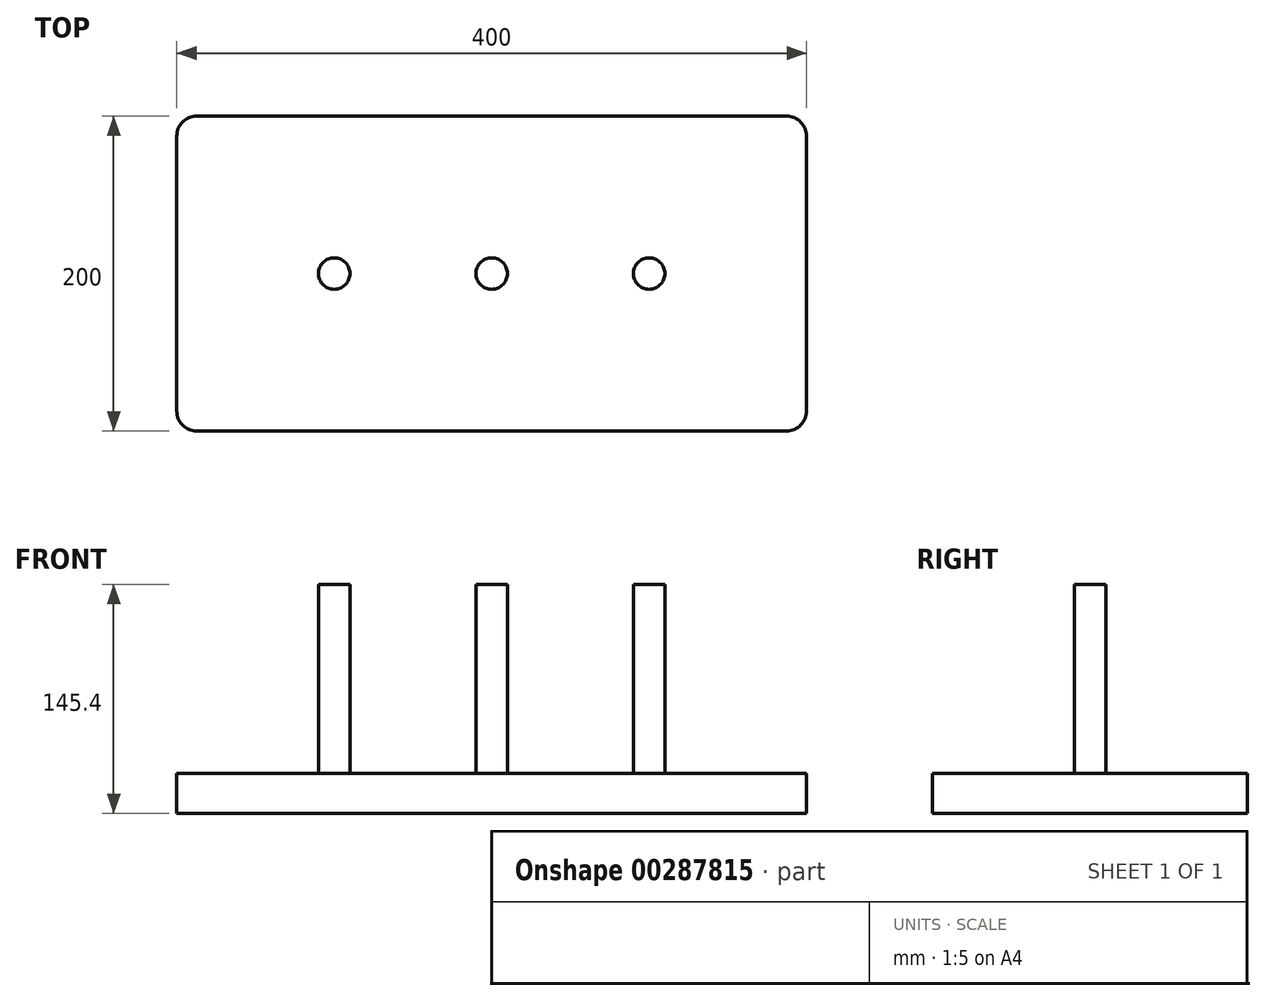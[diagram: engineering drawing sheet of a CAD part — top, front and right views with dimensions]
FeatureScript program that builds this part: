
annotation { "Feature Type Name" : "Feature", "Feature Type Description" : "" }
export const myFeature = defineFeature(function(context is Context, id is Id, definition is map)
    precondition{}
    {
        {
            var Q0;
            Q0=qCreatedBy(makeId("Top.planeOp"),FACE);
            var sketch = newSketch(context, id + "F0", { "sketchPlane" : qUnion([Q0])});
            skLineSegment(sketch, "E0.bottom", {"start": v(200, -100) * mm, "end": v(-200, -100) * mm});
            skLineSegment(sketch, "E0.top", {"start": v(200, 100) * mm, "end": v(-200, 100) * mm});
            skLineSegment(sketch, "E0.left", {"start": v(200, -100) * mm, "end": v(200, 100) * mm});
            skLineSegment(sketch, "E0.right", {"start": v(-200, -100) * mm, "end": v(-200, 100) * mm});
            skPoint(sketch, "E0.middle", {"position": v(0, 0) * mm});
            skSolve(sketch);
        }
        {
            var Q0;
            Q0 = qSketchRegion(id + "F0", true);
            extrude(context, id + "F1", {"entities" : qUnion([Q0]), "depth" : 25.4 * mm});
        }
        {
            var Q0;
            Q0=makeQuery(id+"F1.opExtrude","CAP_FACE",FACE,{"disambiguationData":[OSD([sQuery(id+"F0.wireOp",EDGE,"E0.bottom"),sQuery(id+"F0.wireOp",EDGE,"E0.top"),sQuery(id+"F0.wireOp",EDGE,"E0.left"),sQuery(id+"F0.wireOp",EDGE,"E0.right")])],"isStart":false});
            var sketch = newSketch(context, id + "F2", { "sketchPlane" : qUnion([Q0])});
            skCircle(sketch, "E1", {"center": v(0, 0) * mm, "radius": 10 * mm});
            skCircle(sketch, "E2", {"center": v(100, 0) * mm, "radius": 10 * mm});
            skCircle(sketch, "E3", {"center": v(-100, 0) * mm, "radius": 10 * mm});
            skSolve(sketch);
        }
        {
            var Q0;
            Q0 = qSketchRegion(id + "F2", true);
            extrude(context, id + "F3", {"entities" : qUnion([Q0]), "operationType" : NewBodyOperationType.ADD, "depth" : 120 * mm});
        }
        {
            var Q0;
            Q0=makeQuery(id+"F1.opExtrude","SWEPT_EDGE",EDGE,{"disambiguationData":[OSD([sQuery(id+"F0.wireOp",EDGE,"E0.bottom"),sQuery(id+"F0.wireOp",EDGE,"E0.left")])]});
            var Q1;
            Q1=makeQuery(id+"F1.opExtrude","SWEPT_EDGE",EDGE,{"disambiguationData":[OSD([sQuery(id+"F0.wireOp",EDGE,"E0.bottom"),sQuery(id+"F0.wireOp",EDGE,"E0.right")])]});
            var Q2;
            Q2=makeQuery(id+"F1.opExtrude","SWEPT_EDGE",EDGE,{"disambiguationData":[OSD([sQuery(id+"F0.wireOp",EDGE,"E0.top"),sQuery(id+"F0.wireOp",EDGE,"E0.right")])]});
            var Q3;
            Q3=makeQuery(id+"F1.opExtrude","SWEPT_EDGE",EDGE,{"disambiguationData":[OSD([sQuery(id+"F0.wireOp",EDGE,"E0.top"),sQuery(id+"F0.wireOp",EDGE,"E0.left")])]});
            fillet(context, id + "F4", {"entities" : qUnion([Q0, Q1, Q2, Q3]), "radius" : 12.7 * mm, "tangentPropagation" : true, "allowEdgeOverflow" : false});
        }
    });
